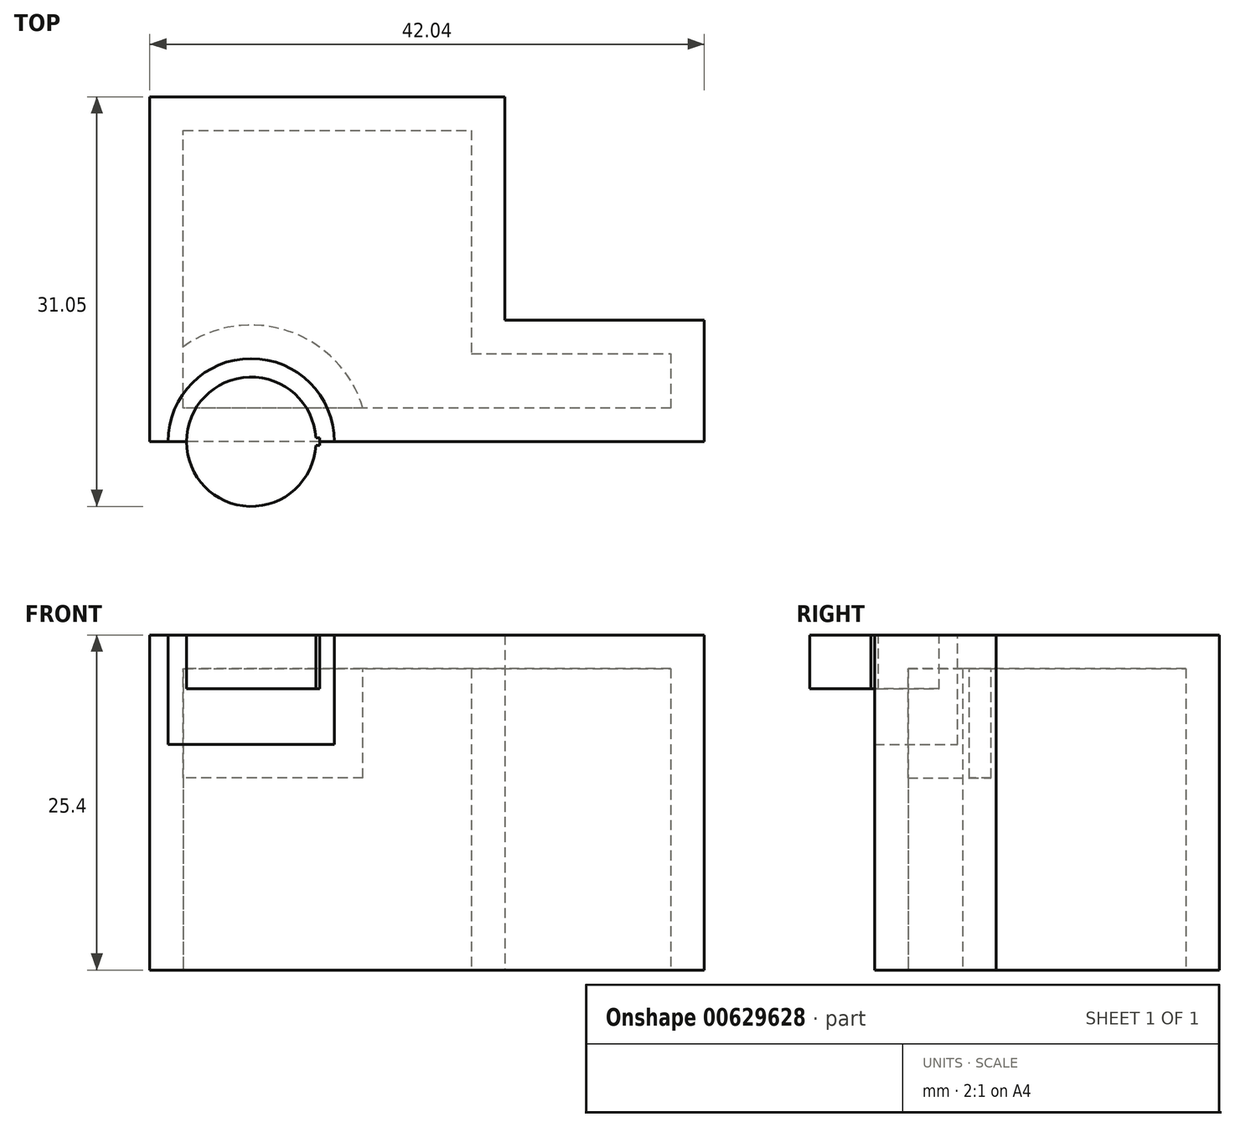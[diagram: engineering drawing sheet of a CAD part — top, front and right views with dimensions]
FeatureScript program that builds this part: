
annotation { "Feature Type Name" : "Feature", "Feature Type Description" : "" }
export const myFeature = defineFeature(function(context is Context, id is Id, definition is map)
    precondition{}
    {
        {
            var Q0;
            Q0=qCreatedBy(makeId("Top.planeOp"),FACE);
            var sketch = newSketch(context, id + "F0", { "sketchPlane" : qUnion([Q0])});
            skLineSegment(sketch, "E0", {"start": v(-32.3, 0) * mm, "end": v(-32.3, 26.15) * mm});
            skLineSegment(sketch, "E1", {"start": v(-32.3, 26.15) * mm, "end": v(-5.38, 26.15) * mm});
            skLineSegment(sketch, "E2", {"start": v(-5.38, 26.15) * mm, "end": v(-5.38, 9.23) * mm});
            skLineSegment(sketch, "E3", {"start": v(-5.38, 9.23) * mm, "end": v(9.74, 9.23) * mm});
            skLineSegment(sketch, "E4", {"start": v(9.74, 9.23) * mm, "end": v(9.74, 0) * mm});
            skLineSegment(sketch, "E5", {"start": v(9.74, 0) * mm, "end": v(-32.3, 0) * mm});
            skSolve(sketch);
        }
        {
            var Q0;
            Q0=makeQuery(id+"F0.imprint","IMPRINT",FACE,{"disambiguationData":[TD([[makeQuery(id+"F0.imprint","IMPRINT",EDGE,{"derivedFrom":sQuery(id+"F0.wireOp",EDGE,"E0")}),-1.0]])]});
            extrude(context, id + "F1", {"entities" : qUnion([Q0]), "depth" : 25.4 * mm, "offsetDistance" : 25.4 * mm});
        }
        {
            var Q0;
            Q0=makeQuery(id+"F1.opExtrude","CAP_FACE",FACE,{"disambiguationData":[OSD([sQuery(id+"F0.wireOp",EDGE,"E0"),sQuery(id+"F0.wireOp",EDGE,"E1"),sQuery(id+"F0.wireOp",EDGE,"E2"),sQuery(id+"F0.wireOp",EDGE,"E3"),sQuery(id+"F0.wireOp",EDGE,"E4"),sQuery(id+"F0.wireOp",EDGE,"E5")])],"isStart":false});
            var sketch = newSketch(context, id + "F2", { "sketchPlane" : qUnion([Q0])});
            skCircle(sketch, "E6", {"center": v(-24.6, 0) * mm, "radius": 6.3 * mm});
            skCircle(sketch, "E7", {"center": v(-24.6, 0) * mm, "radius": 4.9 * mm});
            skSolve(sketch);
        }
        {
            var Q0;
            {var subQ0=sQuery(id+"F2.wireOp",EDGE,"E7");var subQ1=makeQuery(id+"F1.opExtrude","CAP_EDGE",EDGE,{"disambiguationData":[OSD([sQuery(id+"F0.wireOp",EDGE,"E5")])],"isStart":false});var subQ2=makeQuery(id+"F2.imprint","INTERSECT",VERTEX,{"disambiguationData":[OD(0.0)],"derivedFrom":[subQ1,subQ0]});Q0=makeQuery(id+"F2.imprint","IMPRINT",FACE,{"disambiguationData":[TD([[makeQuery(id+"F2.imprint","IMPRINT",EDGE,{"disambiguationData":[TD([[subQ2,1.0]])],"derivedFrom":subQ0}),1.0]])]});}
            var Q1;
            {var subQ0=sQuery(id+"F2.wireOp",EDGE,"E6");var subQ1=makeQuery(id+"F1.opExtrude","CAP_EDGE",EDGE,{"disambiguationData":[OSD([sQuery(id+"F0.wireOp",EDGE,"E5")])],"isStart":false});var subQ2=makeQuery(id+"F2.imprint","INTERSECT",VERTEX,{"disambiguationData":[OD(0.0)],"derivedFrom":[subQ1,subQ0]});Q1=makeQuery(id+"F2.imprint","IMPRINT",FACE,{"disambiguationData":[TD([[makeQuery(id+"F2.imprint","IMPRINT",EDGE,{"disambiguationData":[TD([[subQ2,1.0]])],"derivedFrom":subQ0}),1.0]])]});}
            extrude(context, id + "F3", {"entities" : qUnion([Q0, Q1]), "operationType" : NewBodyOperationType.REMOVE, "oppositeDirection" : true, "depth" : 8.3 * mm, "offsetDistance" : 25.4 * mm});
        }
        {
            var Q0;
            {var subQ0=sQuery(id+"F2.wireOp",EDGE,"E7");var subQ1=makeQuery(id+"F1.opExtrude","CAP_EDGE",EDGE,{"disambiguationData":[OSD([sQuery(id+"F0.wireOp",EDGE,"E5")])],"isStart":false});var subQ2=makeQuery(id+"F2.imprint","INTERSECT",VERTEX,{"disambiguationData":[OD(0.0)],"derivedFrom":[subQ1,subQ0]});Q0=makeQuery(id+"F2.imprint","IMPRINT",FACE,{"disambiguationData":[TD([[makeQuery(id+"F2.imprint","IMPRINT",EDGE,{"disambiguationData":[TD([[subQ2,1.0]])],"derivedFrom":subQ0}),1.0]])]});}
            var Q1;
            {var subQ0=sQuery(id+"F2.wireOp",EDGE,"E7");var subQ1=makeQuery(id+"F1.opExtrude","CAP_EDGE",EDGE,{"disambiguationData":[OSD([sQuery(id+"F0.wireOp",EDGE,"E5")])],"isStart":false});var subQ2=makeQuery(id+"F2.imprint","INTERSECT",VERTEX,{"disambiguationData":[OD(0.0)],"derivedFrom":[subQ1,subQ0]});Q1=makeQuery(id+"F2.imprint","IMPRINT",FACE,{"disambiguationData":[TD([[makeQuery(id+"F2.imprint","IMPRINT",EDGE,{"disambiguationData":[TD([[subQ2,-1.0]])],"derivedFrom":subQ0}),1.0]])]});}
            extrude(context, id + "F4", {"entities" : qUnion([Q0, Q1]), "oppositeDirection" : true, "depth" : 4.1 * mm, "offsetDistance" : 25.4 * mm});
        }
        {
            var Q0;
            {var subQ0=sQuery(id+"F2.wireOp",EDGE,"E7");var subQ1=makeQuery(id+"F1.opExtrude","CAP_EDGE",EDGE,{"disambiguationData":[OSD([sQuery(id+"F0.wireOp",EDGE,"E5")])],"isStart":false});var subQ2=makeQuery(id+"F2.imprint","INTERSECT",VERTEX,{"disambiguationData":[OD(0.0)],"derivedFrom":[subQ1,subQ0]});Q0=makeQuery(id+"F2.imprint","IMPRINT",FACE,{"disambiguationData":[TD([[makeQuery(id+"F2.imprint","IMPRINT",EDGE,{"disambiguationData":[TD([[subQ2,1.0]])],"derivedFrom":subQ0}),1.0]])]});}
            var sketch = newSketch(context, id + "F5", { "sketchPlane" : qUnion([Q0])});
            skLineSegment(sketch, "E8.bottom", {"start": v(-19.42, 0.28) * mm, "end": v(-20.36, 0.28) * mm});
            skLineSegment(sketch, "E8.top", {"start": v(-19.42, -0.28) * mm, "end": v(-20.36, -0.28) * mm});
            skLineSegment(sketch, "E8.left", {"start": v(-19.42, 0.28) * mm, "end": v(-19.42, -0.28) * mm});
            skLineSegment(sketch, "E8.right", {"start": v(-20.36, 0.28) * mm, "end": v(-20.36, -0.28) * mm});
            skPoint(sketch, "E8.middle", {"position": v(-19.9, 0) * mm});
            skSolve(sketch);
        }
        {
            var Q0;
            Q0 = qSketchRegion(id + "F5", true);
            var Q1;
            Q1=makeQuery(id+"F4.opExtrude","CAP_FACE",FACE,{"disambiguationData":[OSD([sQuery(id+"F2.wireOp",EDGE,"E7")])],"isStart":false});
            extrude(context, id + "F6", {"entities" : qUnion([Q0]), "operationType" : NewBodyOperationType.ADD, "endBound" : BoundingType.UP_TO_SURFACE, "oppositeDirection" : true, "depth" : 25.4 * mm, "endBoundEntityFace" : qUnion([Q1]), "offsetDistance" : 25.4 * mm});
        }
        {
            var Q0;
            Q0=makeQuery(id+"F1.opExtrude","CAP_FACE",FACE,{"disambiguationData":[OSD([sQuery(id+"F0.wireOp",EDGE,"E0"),sQuery(id+"F0.wireOp",EDGE,"E1"),sQuery(id+"F0.wireOp",EDGE,"E2"),sQuery(id+"F0.wireOp",EDGE,"E3"),sQuery(id+"F0.wireOp",EDGE,"E4"),sQuery(id+"F0.wireOp",EDGE,"E5")])],"isStart":true});
            shell(context, id + "F7", {"entities" : qUnion([Q0]), "thickness" : 2.54 * mm});
        }
    });
